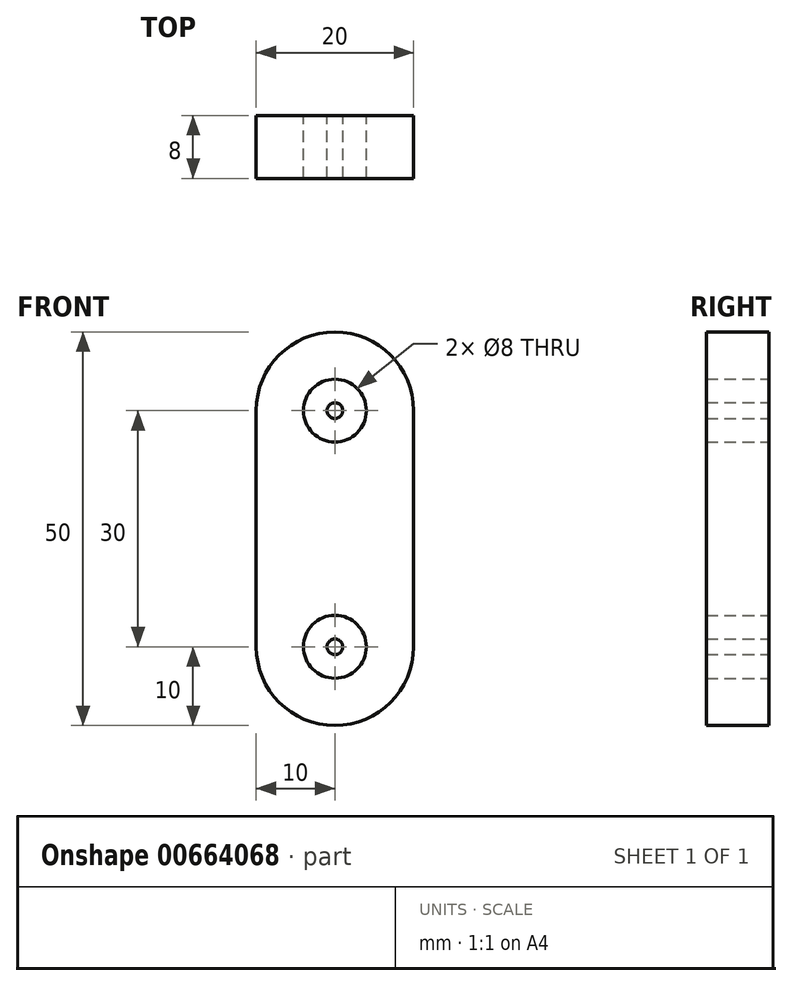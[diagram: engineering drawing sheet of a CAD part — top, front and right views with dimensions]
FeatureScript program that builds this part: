
annotation { "Feature Type Name" : "Feature", "Feature Type Description" : "" }
export const myFeature = defineFeature(function(context is Context, id is Id, definition is map)
    precondition{}
    {
        {
            var Q0;
            Q0=qCreatedBy(makeId("Front.planeOp"),FACE);
            var sketch = newSketch(context, id + "F0", { "sketchPlane" : qUnion([Q0])});
            skCircle(sketch, "E0", {"center": v(0, 0) * mm, "radius": 4 * mm});
            skArc(sketch, "E1", {"start": v(-10, 0) * mm, "mid": v(0, -10) * mm, "end": v(10, 0) * mm});
            skLineSegment(sketch, "E2", {"start": v(-10, 0) * mm, "end": v(-10, 30) * mm});
            skLineSegment(sketch, "E3", {"start": v(10, 0) * mm, "end": v(10, 30) * mm});
            skArc(sketch, "E4", {"start": v(10, 30) * mm, "mid": v(0, 40) * mm, "end": v(-10, 30) * mm});
            skCircle(sketch, "E5", {"center": v(0, 30) * mm, "radius": 4 * mm});
            skSolve(sketch);
        }
        {
            var Q0;
            Q0 = qSketchRegion(id + "F0", true);
            extrude(context, id + "F1", {"entities" : qUnion([Q0]), "depth" : 8 * mm, "offsetDistance" : 25.4 * mm});
        }
        {
            var Q0;
            Q0=qCreatedBy(makeId("Front.planeOp"),FACE);
            var sketch = newSketch(context, id + "F2", { "sketchPlane" : qUnion([Q0])});
            skCircle(sketch, "E6", {"center": v(0, 0) * mm, "radius": 1 * mm});
            skCircle(sketch, "E7", {"center": v(0, 30) * mm, "radius": 1 * mm});
            skSolve(sketch);
        }
        {
            var Q0;
            Q0=makeQuery(id+"F2.imprint","IMPRINT",FACE,{"disambiguationData":[TD([[makeQuery(id+"F2.imprint","IMPRINT",EDGE,{"derivedFrom":sQuery(id+"F2.wireOp",EDGE,"E7")}),1.0]])]});
            var Q1;
            Q1=makeQuery(id+"F2.imprint","IMPRINT",FACE,{"disambiguationData":[TD([[makeQuery(id+"F2.imprint","IMPRINT",EDGE,{"derivedFrom":sQuery(id+"F2.wireOp",EDGE,"E6")}),1.0]])]});
            extrude(context, id + "F3", {"entities" : qUnion([Q0, Q1]), "depth" : 8 * mm, "offsetDistance" : 25.4 * mm});
        }
    });
